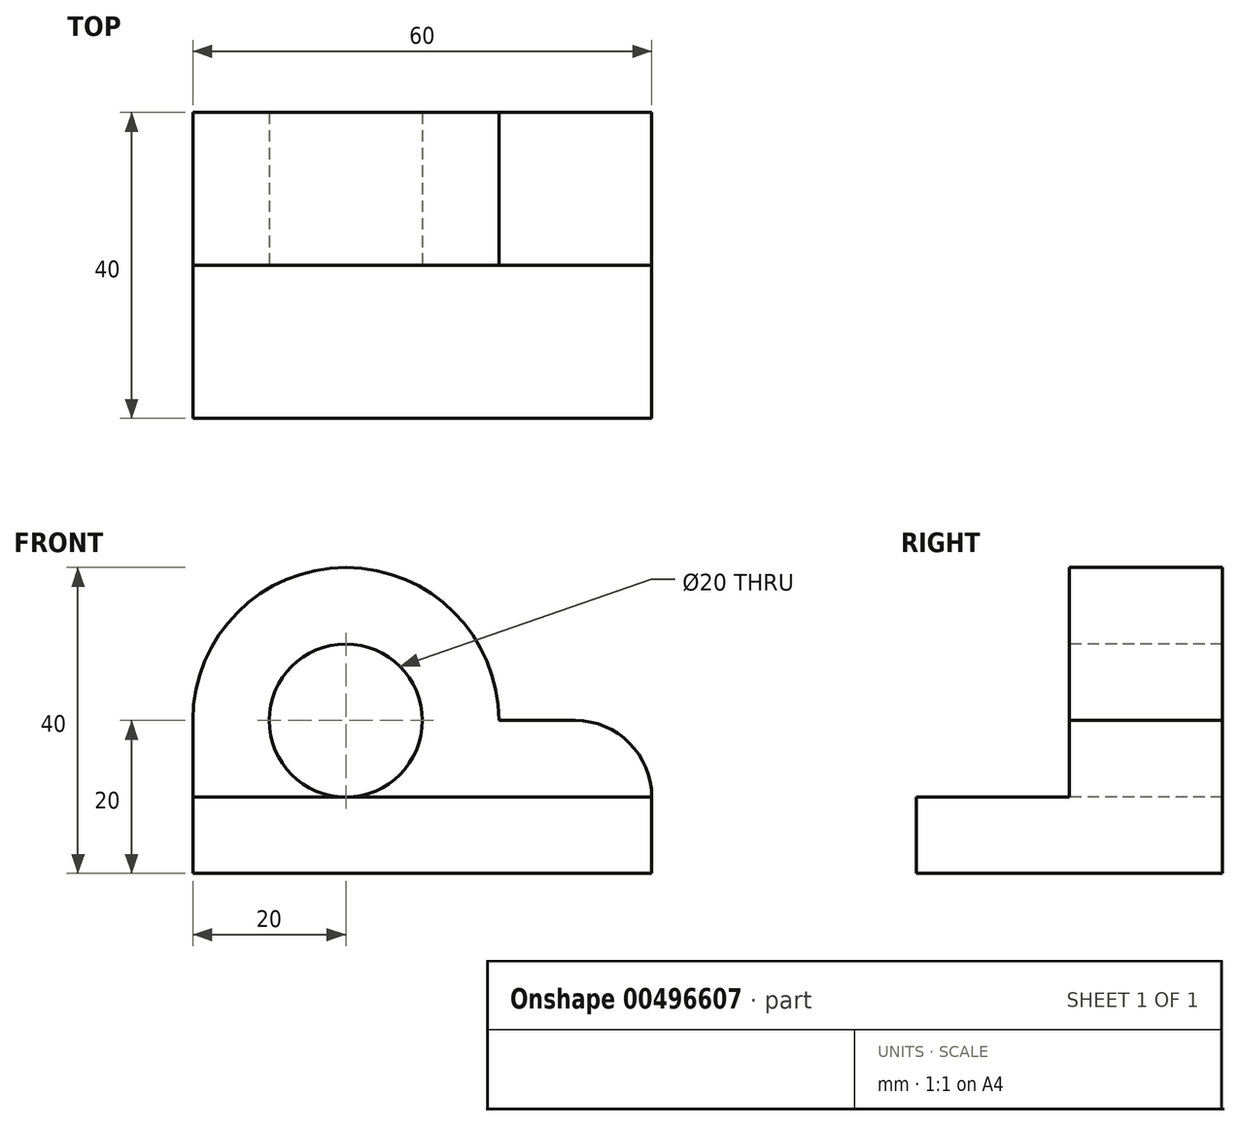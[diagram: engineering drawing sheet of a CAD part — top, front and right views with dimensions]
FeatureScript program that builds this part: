
annotation { "Feature Type Name" : "Feature", "Feature Type Description" : "" }
export const myFeature = defineFeature(function(context is Context, id is Id, definition is map)
    precondition{}
    {
        {
            var Q0;
            Q0=qCreatedBy(makeId("Front.planeOp"),FACE);
            var sketch = newSketch(context, id + "F0", { "sketchPlane" : qUnion([Q0])});
            skLineSegment(sketch, "E0", {"start": v(0, 0) * mm, "end": v(60, 0) * mm});
            skLineSegment(sketch, "E1", {"start": v(60, 0) * mm, "end": v(60, 10) * mm});
            skLineSegment(sketch, "E2", {"start": v(60, 10) * mm, "end": v(0, 10) * mm});
            skLineSegment(sketch, "E3", {"start": v(0, 10) * mm, "end": v(0, 0) * mm});
            skSolve(sketch);
        }
        {
            var Q0;
            Q0=makeQuery(id+"F0.imprint","IMPRINT",FACE,{"disambiguationData":[TD([[makeQuery(id+"F0.imprint","IMPRINT",EDGE,{"derivedFrom":sQuery(id+"F0.wireOp",EDGE,"E0")}),1.0]])]});
            extrude(context, id + "F1", {"entities" : qUnion([Q0]), "depth" : 40 * mm});
        }
        {
            var Q0;
            Q0=makeQuery(id+"F1.opExtrude","SWEPT_FACE",FACE,{"disambiguationData":[OSD([sQuery(id+"F0.wireOp",EDGE,"E2")])]});
            var sketch = newSketch(context, id + "F2", { "sketchPlane" : qUnion([Q0])});
            skLineSegment(sketch, "E4", {"start": v(60, -20) * mm, "end": v(40, -20) * mm});
            skLineSegment(sketch, "E5", {"start": v(40, -20) * mm, "end": v(40, 0) * mm});
            skLineSegment(sketch, "E6", {"start": v(40, 0) * mm, "end": v(60, 0) * mm});
            skLineSegment(sketch, "E7", {"start": v(60, 0) * mm, "end": v(60, -20) * mm});
            skSolve(sketch);
        }
        {
            var Q0;
            Q0=makeQuery(id+"F2.imprint","IMPRINT",FACE,{"disambiguationData":[TD([[makeQuery(id+"F2.imprint","IMPRINT",EDGE,{"derivedFrom":sQuery(id+"F2.wireOp",EDGE,"E4")}),-1.0]])]});
            extrude(context, id + "F3", {"entities" : qUnion([Q0]), "operationType" : NewBodyOperationType.ADD, "depth" : 10 * mm});
        }
        {
            var Q0;
            Q0=makeQuery(id+"F1.opExtrude","SWEPT_FACE",FACE,{"disambiguationData":[OSD([sQuery(id+"F0.wireOp",EDGE,"E2")])]});
            var sketch = newSketch(context, id + "F4", { "sketchPlane" : qUnion([Q0])});
            skLineSegment(sketch, "E8", {"start": v(0, -20) * mm, "end": v(40, -20) * mm});
            skLineSegment(sketch, "E9", {"start": v(40, -20) * mm, "end": v(40, 0) * mm});
            skLineSegment(sketch, "E10", {"start": v(40, 0) * mm, "end": v(0, 0) * mm});
            skLineSegment(sketch, "E11", {"start": v(0, 0) * mm, "end": v(0, -20) * mm});
            skSolve(sketch);
        }
        {
            var Q0;
            Q0=makeQuery(id+"F4.imprint","IMPRINT",FACE,{"disambiguationData":[TD([[makeQuery(id+"F4.imprint","IMPRINT",EDGE,{"derivedFrom":sQuery(id+"F4.wireOp",EDGE,"E8")}),1.0]])]});
            extrude(context, id + "F5", {"entities" : qUnion([Q0]), "operationType" : NewBodyOperationType.ADD, "depth" : 30 * mm});
        }
        {
            var Q0;
            Q0=makeQuery(id+"F3.opExtrude","CAP_EDGE",EDGE,{"disambiguationData":[OSD([sQuery(id+"F2.wireOp",EDGE,"E7")])],"isStart":false});
            fillet(context, id + "F6", {"entities" : qUnion([Q0]), "radius" : 10 * mm, "tangentPropagation" : true, "allowEdgeOverflow" : false});
        }
        {
            var Q0;
            Q0=makeQuery(id+"F5.opExtrude","CAP_EDGE",EDGE,{"disambiguationData":[OSD([sQuery(id+"F4.wireOp",EDGE,"E9")])],"isStart":false});
            var Q1;
            Q1=makeQuery(id+"F5.opExtrude","CAP_EDGE",EDGE,{"disambiguationData":[OSD([sQuery(id+"F4.wireOp",EDGE,"E11")])],"isStart":false});
            fillet(context, id + "F7", {"entities" : qUnion([Q0, Q1]), "radius" : 20 * mm, "tangentPropagation" : true, "allowEdgeOverflow" : false});
        }
        {
            var Q0;
            Q0=makeQuery(id+"F5.boolean.opBoolean","MERGE",FACE,{"derivedFrom":[makeQuery(id+"F3.opExtrude","SWEPT_FACE",FACE,{"disambiguationData":[OSD([sQuery(id+"F2.wireOp",EDGE,"E4")])]}),makeQuery(id+"F5.opExtrude","SWEPT_FACE",FACE,{"disambiguationData":[OSD([sQuery(id+"F4.wireOp",EDGE,"E8")])]})]});
            var sketch = newSketch(context, id + "F8", { "sketchPlane" : qUnion([Q0])});
            skCircle(sketch, "E12", {"center": v(20, 20) * mm, "radius": 10 * mm});
            skSolve(sketch);
        }
        {
            var Q0;
            Q0=makeQuery(id+"F8.imprint","IMPRINT",FACE,{"disambiguationData":[TD([[makeQuery(id+"F8.imprint","IMPRINT",EDGE,{"derivedFrom":sQuery(id+"F8.wireOp",EDGE,"E12")}),1.0]])]});
            extrude(context, id + "F9", {"entities" : qUnion([Q0]), "operationType" : NewBodyOperationType.REMOVE, "oppositeDirection" : true, "depth" : 25 * mm});
        }
    });
